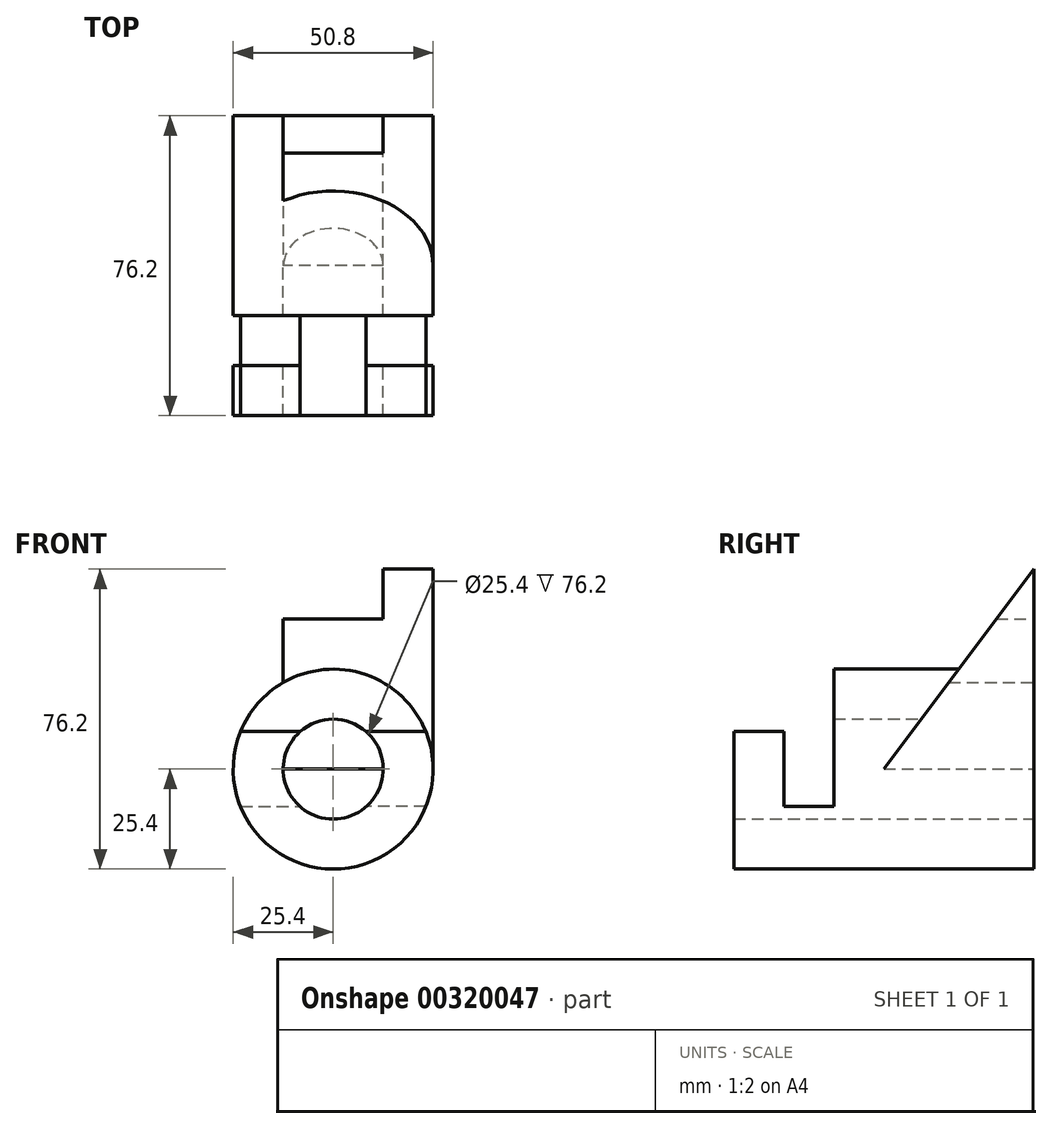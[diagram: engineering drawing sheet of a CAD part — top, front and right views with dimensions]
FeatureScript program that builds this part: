
annotation { "Feature Type Name" : "Feature", "Feature Type Description" : "" }
export const myFeature = defineFeature(function(context is Context, id is Id, definition is map)
    precondition{}
    {
        {
            var Q0;
            Q0=qCreatedBy(makeId("Front.planeOp"),FACE);
            var sketch = newSketch(context, id + "F0", { "sketchPlane" : qUnion([Q0])});
            skCircle(sketch, "E0", {"center": v(0, 0) * mm, "radius": 25.4 * mm});
            skCircle(sketch, "E1", {"center": v(0, 0) * mm, "radius": 12.7 * mm});
            skSolve(sketch);
        }
        {
            var Q0;
            Q0 = qSketchRegion(id + "F0", true);
            extrude(context, id + "F1", {"entities" : qUnion([Q0]), "depth" : 76.2 * mm});
        }
        {
            var Q0;
            Q0=qCreatedBy(makeId("Right.planeOp"),FACE);
            var sketch = newSketch(context, id + "F2", { "sketchPlane" : qUnion([Q0])});
            skLineSegment(sketch, "E2", {"start": v(0, 0) * mm, "end": v(-63.5, 0) * mm});
            skLineSegment(sketch, "E3", {"start": v(-76.2, 9.52) * mm, "end": v(-76.2, 25.4) * mm});
            skLineSegment(sketch, "E4", {"start": v(-76.2, 25.4) * mm, "end": v(-63.5, 25.4) * mm});
            skLineSegment(sketch, "E5", {"start": v(-63.5, 25.4) * mm, "end": v(-63.5, 9.52) * mm});
            skLineSegment(sketch, "E6", {"start": v(-63.5, 9.52) * mm, "end": v(-76.2, 9.52) * mm});
            skLineSegment(sketch, "E7", {"start": v(-76.2, 9.52) * mm, "end": v(-63.5, 9.52) * mm});
            skLineSegment(sketch, "E8", {"start": v(-63.5, 25.4) * mm, "end": v(-50.8, 25.4) * mm});
            skLineSegment(sketch, "E9", {"start": v(-50.8, 25.4) * mm, "end": v(-50.8, -9.53) * mm});
            skLineSegment(sketch, "E10", {"start": v(-50.8, -9.53) * mm, "end": v(-63.5, -9.53) * mm});
            skLineSegment(sketch, "E11", {"start": v(-63.5, -9.53) * mm, "end": v(-63.5, 9.52) * mm});
            skSolve(sketch);
        }
        {
            var Q0;
            Q0 = qSketchRegion(id + "F2", true);
            extrude(context, id + "F3", {"entities" : qUnion([Q0]), "operationType" : NewBodyOperationType.REMOVE, "depth" : 558.8 * mm});
        }
        {
            var Q0;
            Q0=qCreatedBy(makeId("Right.planeOp"),FACE);
            var sketch = newSketch(context, id + "F4", { "sketchPlane" : qUnion([Q0])});
            skLineSegment(sketch, "E12", {"start": v(0, 0) * mm, "end": v(-63.5, 0) * mm});
            skLineSegment(sketch, "E13", {"start": v(-76.2, 9.52) * mm, "end": v(-76.2, 25.4) * mm});
            skLineSegment(sketch, "E14", {"start": v(-76.2, 25.4) * mm, "end": v(-63.5, 25.4) * mm});
            skLineSegment(sketch, "E15", {"start": v(-63.5, 25.4) * mm, "end": v(-63.5, -9.53) * mm});
            skLineSegment(sketch, "E16", {"start": v(-63.5, -9.53) * mm, "end": v(-50.8, -9.53) * mm});
            skLineSegment(sketch, "E17", {"start": v(-50.8, -9.53) * mm, "end": v(-50.8, 25.4) * mm});
            skLineSegment(sketch, "E18", {"start": v(-50.8, 25.4) * mm, "end": v(-63.5, 25.4) * mm});
            skLineSegment(sketch, "E19", {"start": v(-76.2, 25.4) * mm, "end": v(-76.2, 9.52) * mm});
            skLineSegment(sketch, "E20", {"start": v(-76.2, 9.52) * mm, "end": v(-63.5, 9.52) * mm});
            skLineSegment(sketch, "E21", {"start": v(-63.5, 9.52) * mm, "end": v(-63.5, 25.4) * mm});
            skSolve(sketch);
        }
        {
            var Q0;
            Q0 = qSketchRegion(id + "F4", true);
            extrude(context, id + "F5", {"entities" : qUnion([Q0]), "operationType" : NewBodyOperationType.REMOVE, "oppositeDirection" : true, "depth" : 279.4 * mm});
        }
        {
            var Q0;
            Q0=qCreatedBy(makeId("Right.planeOp"),FACE);
            var sketch = newSketch(context, id + "F6", { "sketchPlane" : qUnion([Q0])});
            skLineSegment(sketch, "E22", {"start": v(0, 0) * mm, "end": v(0, 50.8) * mm});
            skLineSegment(sketch, "E23", {"start": v(0, 50.8) * mm, "end": v(0, 0) * mm});
            skLineSegment(sketch, "E24", {"start": v(-38.1, 0) * mm, "end": v(0, 0) * mm});
            skLineSegment(sketch, "E25", {"start": v(-38.1, 0) * mm, "end": v(0, 50.8) * mm});
            skSolve(sketch);
        }
        {
            var Q0;
            Q0 = qSketchRegion(id + "F6", true);
            extrude(context, id + "F7", {"entities" : qUnion([Q0]), "operationType" : NewBodyOperationType.ADD, "depth" : 25.4 * mm});
        }
        {
            var Q0;
            Q0=qCreatedBy(makeId("Right.planeOp"),FACE);
            var sketch = newSketch(context, id + "F8", { "sketchPlane" : qUnion([Q0])});
            skLineSegment(sketch, "E26", {"start": v(0, 0) * mm, "end": v(-38.1, 0) * mm});
            skLineSegment(sketch, "E27", {"start": v(-38.1, 0) * mm, "end": v(0, 0) * mm});
            skLineSegment(sketch, "E28", {"start": v(0, 0) * mm, "end": v(0, 50.8) * mm});
            skLineSegment(sketch, "E29", {"start": v(0, 50.8) * mm, "end": v(-38.1, 0) * mm});
            skSolve(sketch);
        }
        {
            var Q0;
            Q0 = qSketchRegion(id + "F8", true);
            extrude(context, id + "F9", {"entities" : qUnion([Q0]), "operationType" : NewBodyOperationType.ADD, "oppositeDirection" : true, "depth" : 12.7 * mm});
        }
        {
            var Q0;
            Q0=makeQuery(id+"F9.boolean.opBoolean","MERGE",FACE,{"derivedFrom":[makeQuery(id+"F7.boolean.opBoolean","MERGE",FACE,{"derivedFrom":[makeQuery(id+"F1.opExtrude","CAP_FACE",FACE,{"disambiguationData":[OSD([sQuery(id+"F0.wireOp",EDGE,"E0"),sQuery(id+"F0.wireOp",EDGE,"E1")])],"isStart":true}),makeQuery(id+"F7.opExtrude","SWEPT_FACE",FACE,{"disambiguationData":[OSD([sQuery(id+"F6.wireOp",EDGE,"E23")])]})]}),makeQuery(id+"F9.opExtrude","SWEPT_FACE",FACE,{"disambiguationData":[OSD([sQuery(id+"F8.wireOp",EDGE,"E28")])]})]});
            var sketch = newSketch(context, id + "F10", { "sketchPlane" : qUnion([Q0])});
            skLineSegment(sketch, "E30", {"start": v(-25.4, 50.8) * mm, "end": v(-12.7, 50.8) * mm});
            skLineSegment(sketch, "E31", {"start": v(-12.7, 50.8) * mm, "end": v(-12.7, 38.1) * mm});
            skLineSegment(sketch, "E32", {"start": v(-12.7, 38.1) * mm, "end": v(12.7, 38.1) * mm});
            skLineSegment(sketch, "E33", {"start": v(12.7, 38.1) * mm, "end": v(12.7, 50.8) * mm});
            skLineSegment(sketch, "E34", {"start": v(12.7, 50.8) * mm, "end": v(-12.7, 50.8) * mm});
            skSolve(sketch);
        }
        {
            var Q0;
            Q0 = qSketchRegion(id + "F10", true);
            extrude(context, id + "F11", {"entities" : qUnion([Q0]), "operationType" : NewBodyOperationType.REMOVE, "oppositeDirection" : true, "depth" : 25.4 * mm});
        }
    });
